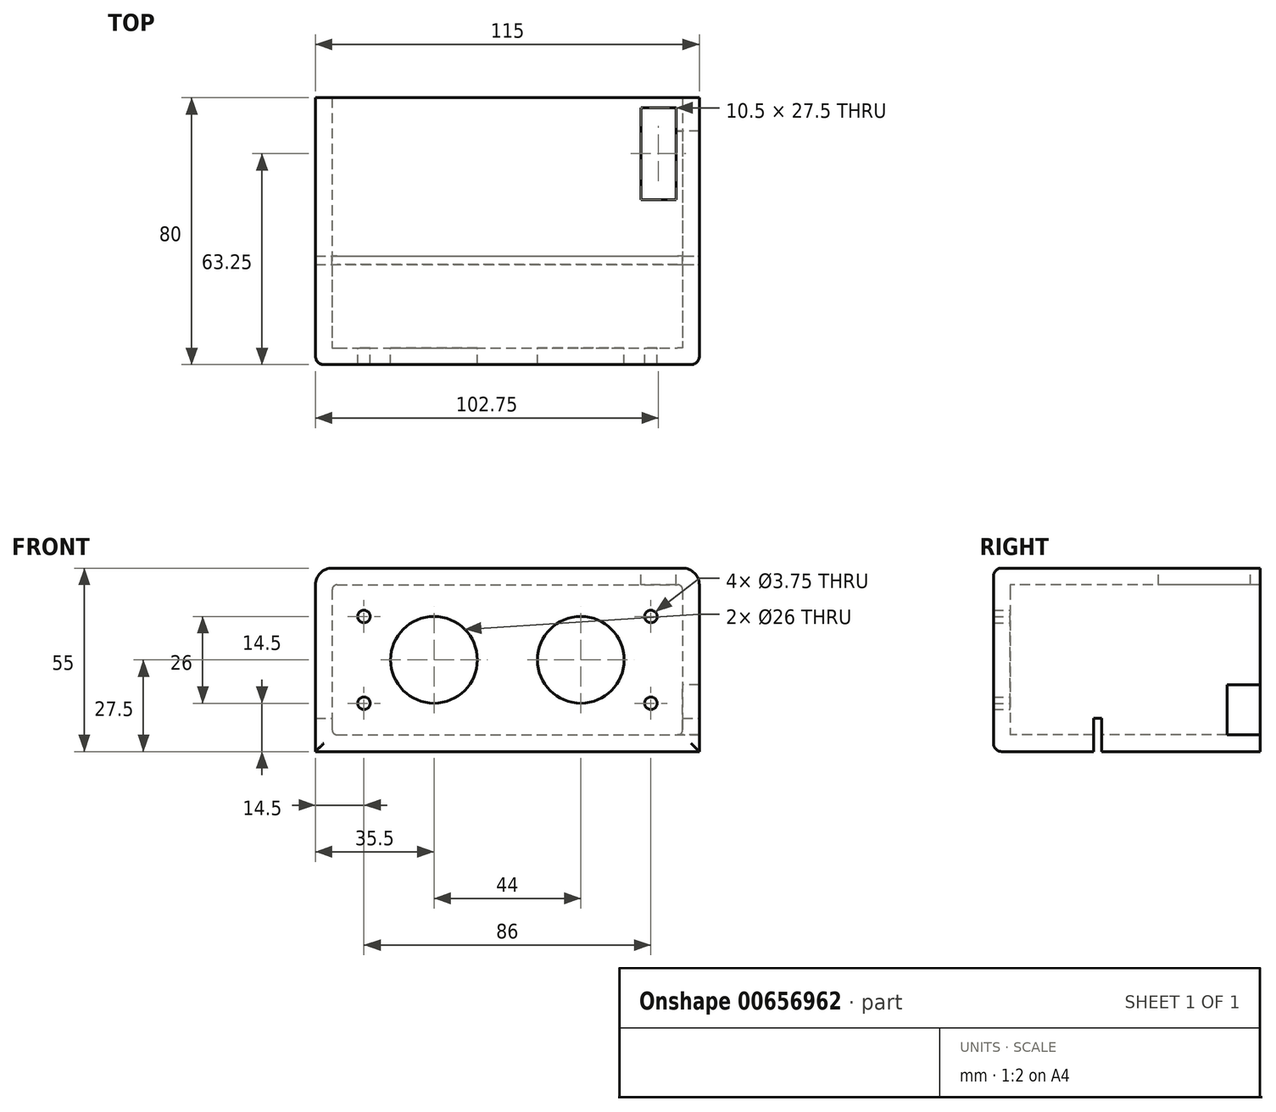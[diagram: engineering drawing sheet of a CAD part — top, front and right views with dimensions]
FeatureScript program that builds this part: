
annotation { "Feature Type Name" : "Feature", "Feature Type Description" : "" }
export const myFeature = defineFeature(function(context is Context, id is Id, definition is map)
    precondition{}
    {
        {
            var Q0;
            Q0=qCreatedBy(makeId("Front.planeOp"),FACE);
            var sketch = newSketch(context, id + "F0", { "sketchPlane" : qUnion([Q0])});
            skLineSegment(sketch, "E0", {"start": v(0, 0) * mm, "end": v(-22, 0) * mm, "construction": true});
            skLineSegment(sketch, "E1", {"start": v(0, 13) * mm, "end": v(-43, 13) * mm, "construction": true});
            skLineSegment(sketch, "E2", {"start": v(0, -13) * mm, "end": v(-43, -13) * mm, "construction": true});
            skLineSegment(sketch, "E3", {"start": v(0, 13) * mm, "end": v(0, 0) * mm, "construction": true});
            skLineSegment(sketch, "E4", {"start": v(0, 0) * mm, "end": v(0, -13) * mm, "construction": true});
            skCircle(sketch, "E5", {"center": v(-43, 13) * mm, "radius": 1.88 * mm});
            skCircle(sketch, "E6", {"center": v(-22, 0) * mm, "radius": 13 * mm});
            skCircle(sketch, "E7", {"center": v(-43, -13) * mm, "radius": 1.88 * mm});
            skLineSegment(sketch, "E8.bottom", {"start": v(-52.5, 22.5) * mm, "end": v(52.5, 22.5) * mm});
            skLineSegment(sketch, "E8.top", {"start": v(-52.5, -22.5) * mm, "end": v(52.5, -22.5) * mm});
            skLineSegment(sketch, "E8.left", {"start": v(-52.5, 22.5) * mm, "end": v(-52.5, -22.5) * mm});
            skLineSegment(sketch, "E8.right", {"start": v(52.5, 22.5) * mm, "end": v(52.5, -22.5) * mm});
            skPoint(sketch, "E8.middle", {"position": v(0, 0) * mm});
            skCircle(sketch, "E9.MirrorC", {"center": v(22, 0) * mm, "radius": 13 * mm});
            skCircle(sketch, "E10.MirrorC", {"center": v(43, 13) * mm, "radius": 1.88 * mm});
            skCircle(sketch, "E11.MirrorC", {"center": v(43, -13) * mm, "radius": 1.88 * mm});
            skSolve(sketch);
        }
        {
            var Q0;
            Q0=makeQuery(id+"F0.imprint","IMPRINT",FACE,{"disambiguationData":[TD([[makeQuery(id+"F0.imprint","IMPRINT",EDGE,{"derivedFrom":sQuery(id+"F0.wireOp",EDGE,"E5")}),-1.0]])]});
            extrude(context, id + "F1", {"entities" : qUnion([Q0]), "depth" : 5 * mm, "offsetDistance" : 25 * mm});
        }
        {
            var Q0;
            Q0=makeQuery(id+"F1.opExtrude","CAP_FACE",FACE,{"disambiguationData":[OSD([sQuery(id+"F0.wireOp",EDGE,"E5"),sQuery(id+"F0.wireOp",EDGE,"E6"),sQuery(id+"F0.wireOp",EDGE,"E7"),sQuery(id+"F0.wireOp",EDGE,"E8.bottom"),sQuery(id+"F0.wireOp",EDGE,"E8.top"),sQuery(id+"F0.wireOp",EDGE,"E8.left"),sQuery(id+"F0.wireOp",EDGE,"E8.right"),sQuery(id+"F0.wireOp",EDGE,"E9.MirrorC"),sQuery(id+"F0.wireOp",EDGE,"E10.MirrorC"),sQuery(id+"F0.wireOp",EDGE,"E11.MirrorC")])],"isStart":false});
            var sketch = newSketch(context, id + "F2", { "sketchPlane" : qUnion([Q0])});
            skLineSegment(sketch, "E12.bottom", {"start": v(-57.5, 27.5) * mm, "end": v(57.5, 27.5) * mm});
            skLineSegment(sketch, "E12.top", {"start": v(-57.5, -27.5) * mm, "end": v(57.5, -27.5) * mm});
            skLineSegment(sketch, "E12.left", {"start": v(-57.5, 27.5) * mm, "end": v(-57.5, -27.5) * mm});
            skLineSegment(sketch, "E12.right", {"start": v(57.5, 27.5) * mm, "end": v(57.5, -27.5) * mm});
            skPoint(sketch, "E12.middle", {"position": v(0, 0) * mm});
            skLineSegment(sketch, "E13.bottom", {"start": v(-52.5, 22.5) * mm, "end": v(52.5, 22.5) * mm});
            skLineSegment(sketch, "E13.top", {"start": v(-52.5, -27.48) * mm, "end": v(52.5, -27.48) * mm});
            skLineSegment(sketch, "E13.left", {"start": v(-52.5, 22.5) * mm, "end": v(-52.5, -27.48) * mm});
            skLineSegment(sketch, "E13.right", {"start": v(52.5, 22.5) * mm, "end": v(52.5, -27.48) * mm});
            skPoint(sketch, "E13.middle", {"position": v(0, -2.5) * mm});
            skSolve(sketch);
        }
        {
            var Q0;
            {var subQ0=sQuery(id+"F2.wireOp",EDGE,"E13.top");Q0=makeQuery(id+"F2.imprint","IMPRINT",FACE,{"disambiguationData":[TD([[makeQuery(id+"F2.imprint","IMPRINT",EDGE,{"derivedFrom":subQ0}),1.0]])]});}
            var Q1;
            Q1=makeQuery(id+"F2.imprint","IMPRINT",FACE,{"disambiguationData":[TD([[makeQuery(id+"F2.imprint","IMPRINT",EDGE,{"derivedFrom":sQuery(id+"F2.wireOp",EDGE,"E12.bottom")}),-1.0]])]});
            extrude(context, id + "F3", {"entities" : qUnion([Q0, Q1]), "operationType" : NewBodyOperationType.ADD, "oppositeDirection" : true, "depth" : 80 * mm, "offsetDistance" : 25 * mm});
        }
        {
            var Q0;
            Q0=makeQuery(id+"F3.opExtrude","SWEPT_FACE",FACE,{"disambiguationData":[OSD([sQuery(id+"F2.wireOp",EDGE,"E12.right")])]});
            var sketch = newSketch(context, id + "F4", { "sketchPlane" : qUnion([Q0])});
            skLineSegment(sketch, "E14", {"start": v(27.5, -27.5) * mm, "end": v(27.5, -17.5) * mm});
            skLineSegment(sketch, "E15", {"start": v(27.5, -17.5) * mm, "end": v(25, -17.5) * mm});
            skLineSegment(sketch, "E16", {"start": v(25, -17.5) * mm, "end": v(25, -27.5) * mm});
            skLineSegment(sketch, "E17", {"start": v(25, -27.5) * mm, "end": v(27.5, -27.5) * mm});
            skSolve(sketch);
        }
        {
            var Q0;
            Q0 = qSketchRegion(id + "F4", true);
            extrude(context, id + "F5", {"entities" : qUnion([Q0]), "operationType" : NewBodyOperationType.REMOVE, "endBound" : BoundingType.THROUGH_ALL, "oppositeDirection" : true, "depth" : 25 * mm, "offsetDistance" : 25 * mm});
        }
        {
            var Q0;
            Q0=makeQuery(id+"F3.opExtrude","CAP_EDGE",EDGE,{"disambiguationData":[OSD([sQuery(id+"F2.wireOp",EDGE,"E12.bottom")])],"isStart":true});
            var Q1;
            Q1=makeQuery(id+"F3.opExtrude","CAP_EDGE",EDGE,{"disambiguationData":[OSD([sQuery(id+"F2.wireOp",EDGE,"E12.left")])],"isStart":true});
            var Q2;
            Q2=makeQuery(id+"F3.opExtrude","CAP_EDGE",EDGE,{"disambiguationData":[OSD([sQuery(id+"F2.wireOp",EDGE,"E12.top")])],"isStart":true});
            var Q3;
            Q3=makeQuery(id+"F3.opExtrude","CAP_EDGE",EDGE,{"disambiguationData":[OSD([sQuery(id+"F2.wireOp",EDGE,"E12.right")])],"isStart":true});
            fillet(context, id + "F6", {"entities" : qUnion([Q0, Q1, Q2, Q3]), "radius" : 2.5 * mm, "tangentPropagation" : true, "allowEdgeOverflow" : false});
        }
        {
            var Q0;
            Q0=makeQuery(id+"F3.opExtrude","SWEPT_EDGE",EDGE,{"disambiguationData":[OSD([sQuery(id+"F2.wireOp",EDGE,"E12.bottom"),sQuery(id+"F2.wireOp",EDGE,"E12.left")])]});
            var Q1;
            Q1=makeQuery(id+"F3.opExtrude","SWEPT_EDGE",EDGE,{"disambiguationData":[OSD([sQuery(id+"F2.wireOp",EDGE,"E12.bottom"),sQuery(id+"F2.wireOp",EDGE,"E12.right")])]});
            fillet(context, id + "F7", {"entities" : qUnion([Q0, Q1]), "radius" : 5 * mm, "tangentPropagation" : true, "allowEdgeOverflow" : false});
        }
        {
            var Q0;
            Q0=makeQuery(id+"F3.opExtrude","SWEPT_FACE",FACE,{"disambiguationData":[OSD([sQuery(id+"F2.wireOp",EDGE,"E12.bottom")])]});
            var sketch = newSketch(context, id + "F8", { "sketchPlane" : qUnion([Q0])});
            skLineSegment(sketch, "E18.bottom", {"start": v(50.5, 72) * mm, "end": v(40, 72) * mm});
            skLineSegment(sketch, "E18.top", {"start": v(50.5, 44.5) * mm, "end": v(40, 44.5) * mm});
            skLineSegment(sketch, "E18.left", {"start": v(50.5, 72) * mm, "end": v(50.5, 44.5) * mm});
            skLineSegment(sketch, "E18.right", {"start": v(40, 72) * mm, "end": v(40, 44.5) * mm});
            skSolve(sketch);
        }
        {
            var Q0;
            Q0 = qSketchRegion(id + "F8", true);
            var Q1;
            Q1=makeQuery(id+"F3.opExtrude","SWEPT_FACE",FACE,{"disambiguationData":[OSD([sQuery(id+"F2.wireOp",EDGE,"E13.bottom")])]});
            extrude(context, id + "F9", {"entities" : qUnion([Q0]), "operationType" : NewBodyOperationType.REMOVE, "endBound" : BoundingType.UP_TO_SURFACE, "oppositeDirection" : true, "depth" : 25 * mm, "endBoundEntityFace" : qUnion([Q1]), "offsetDistance" : 25 * mm});
        }
        {
            var Q0;
            Q0=makeQuery(id+"F3.opExtrude","SWEPT_FACE",FACE,{"disambiguationData":[OSD([sQuery(id+"F2.wireOp",EDGE,"E13.right")])]});
            var sketch = newSketch(context, id + "F10", { "sketchPlane" : qUnion([Q0])});
            skLineSegment(sketch, "E19.bottom", {"start": v(-75, -22.5) * mm, "end": v(-65, -22.5) * mm});
            skLineSegment(sketch, "E19.top", {"start": v(-75, -7.5) * mm, "end": v(-65, -7.5) * mm});
            skLineSegment(sketch, "E19.left", {"start": v(-75, -22.5) * mm, "end": v(-75, -7.5) * mm});
            skLineSegment(sketch, "E19.right", {"start": v(-65, -22.5) * mm, "end": v(-65, -7.5) * mm});
            skSolve(sketch);
        }
        {
            var Q0;
            Q0 = qSketchRegion(id + "F10", true);
            extrude(context, id + "F11", {"entities" : qUnion([Q0]), "operationType" : NewBodyOperationType.REMOVE, "endBound" : BoundingType.THROUGH_ALL, "oppositeDirection" : true, "depth" : 25 * mm, "offsetDistance" : 25 * mm});
        }
        {
            var Q0;
            Q0=makeQuery(id+"F1.opExtrude","CAP_EDGE",EDGE,{"disambiguationData":[OSD([sQuery(id+"F0.wireOp",EDGE,"E8.top")])],"isStart":true});
            var Q1;
            Q1=makeQuery(id+"F1.opExtrude","CAP_EDGE",EDGE,{"disambiguationData":[OSD([sQuery(id+"F0.wireOp",EDGE,"E8.right")])],"isStart":true});
            var Q2;
            Q2=makeQuery(id+"F1.opExtrude","CAP_EDGE",EDGE,{"disambiguationData":[OSD([sQuery(id+"F0.wireOp",EDGE,"E8.bottom")])],"isStart":true});
            var Q3;
            Q3=makeQuery(id+"F1.opExtrude","CAP_EDGE",EDGE,{"disambiguationData":[OSD([sQuery(id+"F0.wireOp",EDGE,"E8.left")])],"isStart":true});
            var Q4;
            Q4=makeQuery(id+"F3.opExtrude","SWEPT_EDGE",EDGE,{"disambiguationData":[OSD([sQuery(id+"F2.wireOp",EDGE,"E13.bottom"),sQuery(id+"F2.wireOp",EDGE,"E13.left")])]});
            var Q5;
            Q5=makeQuery(id+"F3.opExtrude","SWEPT_EDGE",EDGE,{"disambiguationData":[OSD([sQuery(id+"F2.wireOp",EDGE,"E13.bottom"),sQuery(id+"F2.wireOp",EDGE,"E13.right")])]});
            var Q6;
            {var subQ0=sQuery(id+"F0.wireOp",EDGE,"E8.top");var subQ1=sQuery(id+"F2.wireOp",EDGE,"E13.right");Q6=makeQuery(id+"F5.boolean.opBoolean","SPLIT",EDGE,{"disambiguationData":[TD([makeQuery(id+"F5.opExtrude","SWEPT_FACE",FACE,{"disambiguationData":[OSD([sQuery(id+"F4.wireOp",EDGE,"E16")])]})])],"derivedFrom":makeQuery(id+"F3.opExtrude","SWEPT_EDGE",EDGE,{"disambiguationData":[OSD([subQ0,subQ1])]})});}
            var Q7;
            {var subQ0=sQuery(id+"F2.wireOp",EDGE,"E13.right");var subQ1=sQuery(id+"F0.wireOp",EDGE,"E8.top");Q7=makeQuery(id+"F5.boolean.opBoolean","SPLIT",EDGE,{"disambiguationData":[TD([makeQuery(id+"F5.opExtrude","SWEPT_FACE",FACE,{"disambiguationData":[OSD([sQuery(id+"F4.wireOp",EDGE,"E14")])]})])],"derivedFrom":makeQuery(id+"F3.opExtrude","SWEPT_EDGE",EDGE,{"disambiguationData":[OSD([subQ1,subQ0])]})});}
            var Q8;
            {var subQ0=sQuery(id+"F0.wireOp",EDGE,"E8.top");var subQ1=sQuery(id+"F2.wireOp",EDGE,"E13.left");Q8=makeQuery(id+"F5.boolean.opBoolean","SPLIT",EDGE,{"disambiguationData":[TD([makeQuery(id+"F5.opExtrude","SWEPT_FACE",FACE,{"disambiguationData":[OSD([sQuery(id+"F4.wireOp",EDGE,"E16")])]})])],"derivedFrom":makeQuery(id+"F3.opExtrude","SWEPT_EDGE",EDGE,{"disambiguationData":[OSD([subQ0,subQ1])]})});}
            var Q9;
            {var subQ0=sQuery(id+"F2.wireOp",EDGE,"E13.left");var subQ1=sQuery(id+"F0.wireOp",EDGE,"E8.top");Q9=makeQuery(id+"F5.boolean.opBoolean","SPLIT",EDGE,{"disambiguationData":[TD([makeQuery(id+"F5.opExtrude","SWEPT_FACE",FACE,{"disambiguationData":[OSD([sQuery(id+"F4.wireOp",EDGE,"E14")])]})])],"derivedFrom":makeQuery(id+"F3.opExtrude","SWEPT_EDGE",EDGE,{"disambiguationData":[OSD([subQ1,subQ0])]})});}
            fillet(context, id + "F12", {"entities" : qUnion([Q0, Q1, Q2, Q3, Q4, Q5, Q6, Q7, Q8, Q9]), "radius" : 1.5 * mm, "tangentPropagation" : true, "allowEdgeOverflow" : false});
        }
    });
